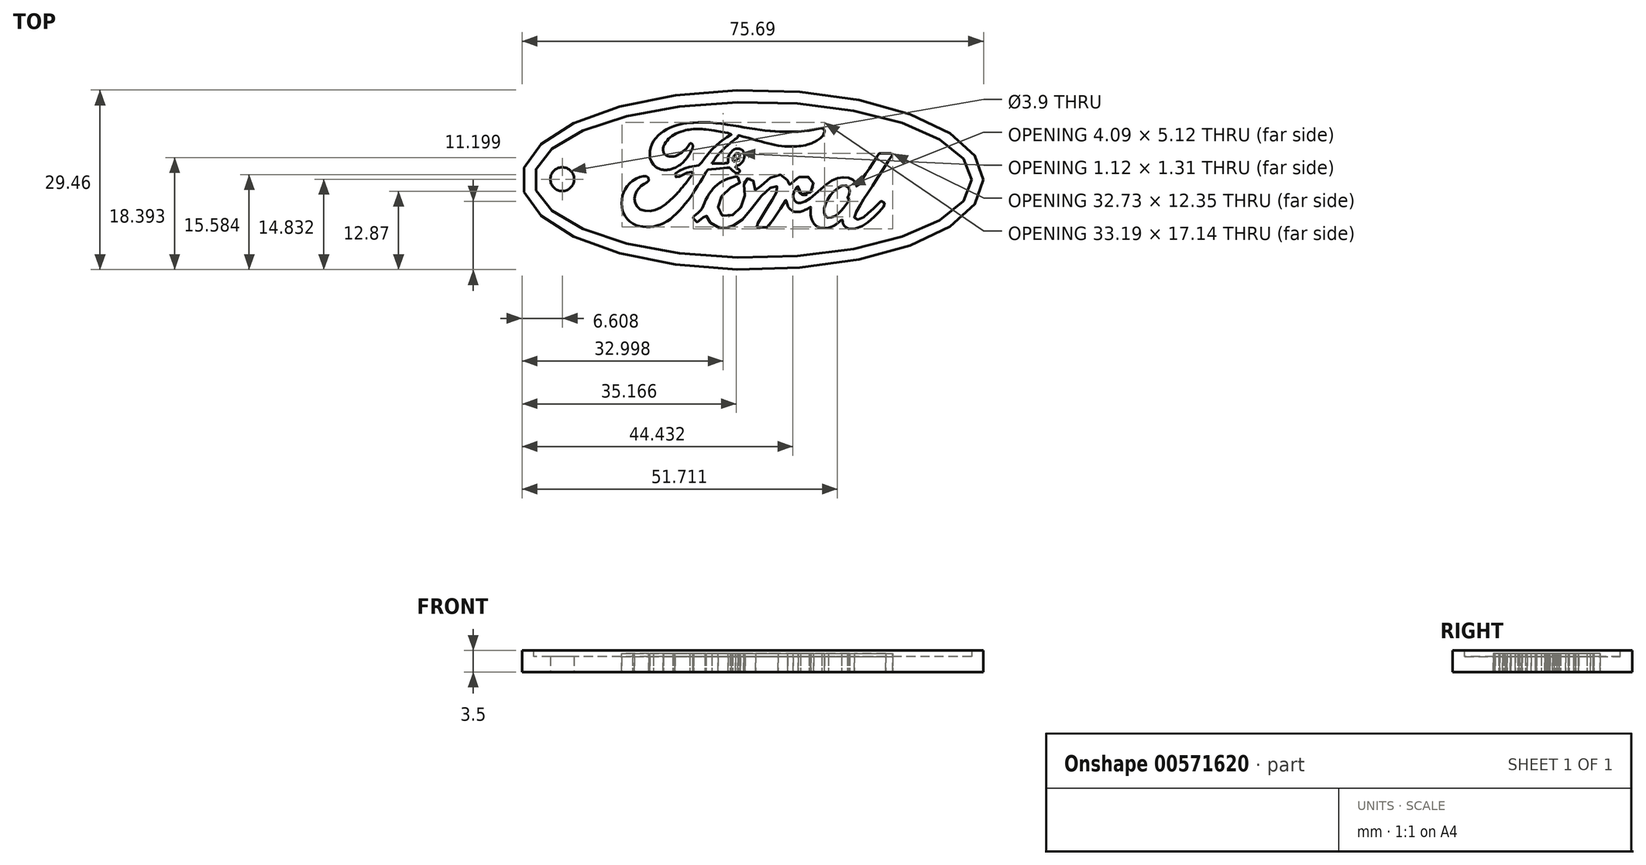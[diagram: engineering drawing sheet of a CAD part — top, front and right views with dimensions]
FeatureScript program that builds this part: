
annotation { "Feature Type Name" : "Feature", "Feature Type Description" : "" }
export const myFeature = defineFeature(function(context is Context, id is Id, definition is map)
    precondition{}
    {
        {
            var Q0;
            Q0=qCreatedBy(makeId("Top.planeOp"),FACE);
            var sketch = newSketch(context, id + "F0", { "sketchPlane" : qUnion([Q0])});
            skEllipse(sketch, "E0", {"center": v(49.35, 28.07) * mm, "majorRadius": 37.84 * mm, "minorRadius": 14.73 * mm, "majorAxis": v(1, 0)});
            skEllipse(sketch, "E1", {"center": v(49.35, 28.07) * mm, "majorRadius": 35.9 * mm, "minorRadius": 12.78 * mm, "majorAxis": v(1, 0)});
            skEllipse(sketch, "E2", {"center": v(49.35, 28.07) * mm, "majorRadius": 34.5 * mm, "minorRadius": 11.46 * mm, "majorAxis": v(1, 0)});
            skFitSpline(sketch, "E3", {"points": [v(39, 33.96) * mm, v(38.65, 33.42) * mm, v(37.9, 32.72) * mm, v(36.9, 32.06) * mm, v(36.02, 31.87) * mm, v(35.3, 32) * mm, v(34.74, 32.53) * mm, v(34.71, 33.54) * mm], "startDerivative": vector(-2.54, -4.41) * mm, "endDerivative": vector(0.86, 7.14) * mm});
            skFitSpline(sketch, "E4", {"points": [v(39, 33.96) * mm, v(39.05, 34.01) * mm, v(39.13, 34.04) * mm, v(39.22, 34.04) * mm, v(39.33, 34) * mm, v(39.41, 33.95) * mm, v(39.48, 33.85) * mm, v(39.52, 33.7) * mm, v(39.53, 33.58) * mm, v(39.51, 33.42) * mm, v(39.47, 33.25) * mm], "startDerivative": vector(0.5, 0.77) * mm, "endDerivative": vector(-0.4, -1.33) * mm});
            skFitSpline(sketch, "E5", {"points": [v(39.47, 33.25) * mm, v(39.38, 33.05) * mm, v(39.2, 32.68) * mm, v(39.06, 32.43) * mm, v(38.93, 32.22) * mm, v(38.79, 32) * mm, v(38.53, 31.64) * mm, v(38.31, 31.37) * mm, v(37.94, 30.96) * mm, v(37.5, 30.58) * mm, v(37.15, 30.34) * mm, v(36.73, 30.1) * mm, v(36.23, 29.9) * mm], "startDerivative": vector(-1.36, -2.97) * mm, "endDerivative": vector(-5.23, -2.02) * mm});
            skFitSpline(sketch, "E6", {"points": [v(36.23, 29.9) * mm, v(36.02, 29.83) * mm, v(35.62, 29.74) * mm, v(35.12, 29.7) * mm, v(34.65, 29.7) * mm, v(34.25, 29.8) * mm, v(33.78, 29.96) * mm, v(33.42, 30.23) * mm, v(33.06, 30.54) * mm], "startDerivative": vector(-2.14, -0.8) * mm, "endDerivative": vector(-2.8, 2.34) * mm});
            skFitSpline(sketch, "E7", {"points": [v(33.06, 30.54) * mm, v(32.87, 30.8) * mm, v(32.58, 31.42) * mm, v(32.5, 31.71) * mm, v(32.47, 32.08) * mm, v(32.47, 32.6) * mm, v(32.5, 32.94) * mm, v(32.6, 33.35) * mm, v(32.72, 33.73) * mm, v(32.9, 34.16) * mm, v(33.15, 34.52) * mm, v(33.4, 34.86) * mm, v(33.8, 35.29) * mm, v(34.05, 35.52) * mm, v(34.32, 35.72) * mm, v(34.58, 35.93) * mm, v(34.9, 36.13) * mm, v(35.32, 36.36) * mm, v(35.67, 36.53) * mm, v(36.14, 36.74) * mm, v(36.63, 36.92) * mm, v(37.04, 37.04) * mm, v(37.3, 37.12) * mm, v(37.67, 37.22) * mm, v(38.03, 37.28) * mm, v(38.4, 37.35) * mm, v(38.78, 37.38) * mm, v(39.14, 37.41) * mm, v(39.67, 37.44) * mm, v(40.22, 37.47) * mm, v(40.68, 37.48) * mm, v(41.09, 37.5) * mm, v(41.53, 37.5) * mm], "startDerivative": vector(-6.48, 7.74) * mm, "endDerivative": vector(14.01, -0.13) * mm});
            skFitSpline(sketch, "E8", {"points": [v(41.53, 37.5) * mm, v(41.84, 37.5) * mm, v(42.37, 37.45) * mm, v(42.84, 37.42) * mm, v(43.37, 37.36) * mm, v(43.76, 37.3) * mm, v(44.34, 37.25) * mm, v(44.92, 37.17) * mm, v(45.59, 37.07) * mm, v(46.15, 36.97) * mm, v(46.53, 36.9) * mm, v(47.04, 36.82) * mm, v(47.56, 36.73) * mm, v(47.96, 36.66) * mm, v(48.43, 36.59) * mm, v(48.95, 36.51) * mm, v(49.49, 36.44) * mm, v(49.85, 36.38) * mm, v(50.28, 36.3) * mm, v(50.76, 36.24) * mm, v(51.13, 36.2) * mm, v(51.49, 36.15) * mm, v(51.98, 36.1) * mm, v(52.43, 36.05) * mm, v(52.87, 36.01) * mm, v(53.18, 35.98) * mm, v(53.5, 35.97) * mm, v(53.87, 35.95) * mm, v(54.32, 35.94) * mm, v(54.77, 35.94) * mm, v(55.14, 35.94) * mm, v(55.42, 35.94) * mm, v(55.7, 35.94) * mm, v(56.13, 35.95) * mm, v(56.44, 35.96) * mm, v(56.66, 35.97) * mm, v(56.92, 35.99) * mm, v(57.53, 36.03) * mm, v(58.03, 36.08) * mm, v(58.43, 36.13) * mm, v(58.76, 36.18) * mm, v(59, 36.22) * mm, v(59.27, 36.27) * mm, v(59.5, 36.31) * mm, v(59.74, 36.36) * mm, v(59.93, 36.4) * mm, v(60.14, 36.44) * mm, v(60.65, 36.52) * mm], "startDerivative": vector(15.58, 0.37) * mm, "endDerivative": vector(12.01, -0.51) * mm});
            skFitSpline(sketch, "E9", {"points": [v(60.65, 36.52) * mm, v(60.76, 36.52) * mm, v(60.84, 36.49) * mm, v(60.9, 36.44) * mm, v(60.97, 36.39) * mm, v(61.04, 36.3) * mm, v(61.07, 36.22) * mm, v(61.1, 36.1) * mm, v(61.1, 35.95) * mm, v(61.1, 35.85) * mm, v(61.04, 35.67) * mm, v(60.95, 35.46) * mm, v(60.81, 35.27) * mm, v(60.72, 35.16) * mm, v(60.58, 35.02) * mm, v(60.42, 34.89) * mm, v(60.2, 34.72) * mm, v(60, 34.6) * mm, v(59.84, 34.5) * mm, v(59.69, 34.4) * mm, v(59.5, 34.3) * mm, v(59.31, 34.2) * mm, v(59.14, 34.13) * mm, v(58.92, 34.04) * mm, v(58.56, 33.9) * mm], "startDerivative": vector(3.4, 0.28) * mm, "endDerivative": vector(-3.98, -1.68) * mm});
            skFitSpline(sketch, "E10", {"points": [v(58.56, 33.9) * mm, v(58.35, 33.84) * mm, v(58.07, 33.77) * mm, v(57.54, 33.67) * mm, v(57.1, 33.62) * mm, v(56.58, 33.57) * mm, v(56.12, 33.53) * mm, v(55.07, 33.53) * mm, v(54.11, 33.6) * mm, v(53, 33.8) * mm, v(51.9, 34.04) * mm, v(50.74, 34.36) * mm, v(49.2, 34.77) * mm, v(47.16, 35.3) * mm, v(46.92, 35.34) * mm], "startDerivative": vector(-5.59, -1.45) * mm, "endDerivative": vector(-4.29, 0.33) * mm});
            skFitSpline(sketch, "E11", {"points": [v(46.92, 35.34) * mm, v(46.92, 35.08) * mm, v(46.85, 34.96) * mm, v(46.52, 34.77) * mm, v(46.23, 34.53) * mm, v(45.97, 34.34) * mm, v(45.45, 33.9) * mm, v(45.1, 33.6) * mm, v(44.65, 33.21) * mm, v(44.15, 32.71) * mm, v(43.8, 32.35) * mm, v(43.3, 31.72) * mm, v(43.04, 31.34) * mm, v(42.76, 30.9) * mm, v(42.66, 30.7) * mm], "startDerivative": vector(0.32, -5.23) * mm, "endDerivative": vector(-1.72, -3.44) * mm});
            skFitSpline(sketch, "E12", {"points": [v(42.66, 30.7) * mm, v(43.28, 30.77) * mm, v(44, 30.77) * mm, v(44.55, 30.77) * mm, v(44.83, 30.79) * mm, v(45.06, 30.8) * mm, v(45.27, 30.83) * mm, v(45.3, 30.84) * mm, v(45.31, 31.17) * mm, v(45.31, 31.57) * mm, v(45.48, 32.15) * mm, v(45.94, 32.73) * mm, v(46.55, 33.13) * mm, v(47.15, 33.17) * mm], "startDerivative": vector(6.55, 0.78) * mm, "endDerivative": vector(6.66, -0.32) * mm});
            skFitSpline(sketch, "E13", {"points": [v(47.15, 33.17) * mm, v(47.47, 33.05) * mm, v(47.86, 32.67) * mm, v(48.01, 32.21) * mm, v(47.98, 31.74) * mm, v(47.78, 31.2) * mm, v(47.44, 30.77) * mm, v(47.15, 30.55) * mm, v(46.8, 30.37) * mm, v(46.52, 30.25) * mm], "startDerivative": vector(3.19, -0.8) * mm, "endDerivative": vector(-2.79, -1.33) * mm});
            skFitSpline(sketch, "E14", {"points": [v(46.52, 30.25) * mm, v(46.52, 30.14) * mm, v(46.8, 29.93) * mm, v(47.03, 29.78) * mm, v(47.15, 29.66) * mm, v(47.25, 29.58) * mm, v(47.22, 29.38) * mm, v(47.03, 29.19) * mm, v(46.76, 29.15) * mm, v(46.42, 29.31) * mm, v(46.13, 29.53) * mm, v(45.86, 29.76) * mm, v(45.67, 29.95) * mm, v(45.61, 30.05) * mm], "startDerivative": vector(-0.59, -2.04) * mm, "endDerivative": vector(-0.87, 1.8) * mm});
            skFitSpline(sketch, "E15", {"points": [v(45.61, 30.05) * mm, v(45.41, 30.05) * mm, v(45.06, 30.05) * mm, v(44.63, 29.98) * mm, v(44.26, 29.95) * mm, v(43.7, 29.9) * mm, v(43.21, 29.83) * mm, v(42.53, 29.78) * mm, v(42.06, 29.71) * mm, v(41.92, 29.67) * mm, v(41.74, 29.37) * mm, v(41.5, 28.97) * mm, v(41.19, 28.44) * mm, v(40.99, 28.13) * mm, v(40.74, 27.74) * mm, v(40.33, 27.06) * mm, v(39.87, 26.39) * mm, v(39.59, 25.91) * mm, v(39.28, 25.45) * mm, v(38.97, 25.01) * mm, v(38.67, 24.62) * mm, v(38.17, 24.01) * mm, v(37.74, 23.49) * mm, v(37.39, 23.08) * mm, v(36.87, 22.57) * mm, v(36.46, 22.17) * mm, v(36.04, 21.81) * mm, v(35.72, 21.54) * mm, v(35.34, 21.28) * mm, v(34.65, 20.91) * mm], "startDerivative": vector(-8.68, -0.14) * mm, "endDerivative": vector(-17.37, -8.98) * mm});
            skFitSpline(sketch, "E16", {"points": [v(34.65, 20.91) * mm, v(34.31, 20.76) * mm, v(33.82, 20.6) * mm, v(33.29, 20.46) * mm, v(32.61, 20.35) * mm, v(32.01, 20.31) * mm, v(31.4, 20.36) * mm, v(30.81, 20.44) * mm, v(30.32, 20.59) * mm, v(29.86, 20.79) * mm, v(29.27, 21.19) * mm, v(28.86, 21.55) * mm, v(28.48, 22.05) * mm, v(28.24, 22.49) * mm, v(28.03, 22.96) * mm, v(27.93, 23.34) * mm, v(27.86, 23.94) * mm, v(27.88, 24.74) * mm, v(28, 25.46) * mm, v(28.16, 25.96) * mm, v(28.4, 26.45) * mm, v(28.73, 26.96) * mm, v(29.2, 27.48) * mm, v(29.63, 27.87) * mm], "startDerivative": vector(-9.1, -4.58) * mm, "endDerivative": vector(9.88, 8.35) * mm});
            skFitSpline(sketch, "E17", {"points": [v(29.63, 27.87) * mm, v(30.22, 28.25) * mm, v(30.65, 28.44) * mm, v(31.2, 28.62) * mm, v(31.5, 28.68) * mm, v(31.85, 28.65) * mm, v(32.09, 28.57) * mm, v(32.25, 28.4) * mm, v(32.3, 28.17) * mm, v(32.3, 27.92) * mm, v(32.09, 27.7) * mm, v(31.78, 27.55) * mm, v(31.48, 27.37) * mm, v(31.12, 27.1) * mm, v(30.89, 26.87) * mm, v(30.64, 26.62) * mm, v(30.36, 26.27) * mm, v(30.09, 25.66) * mm, v(29.98, 25.3) * mm, v(29.98, 24.6) * mm, v(30.19, 24.06) * mm, v(30.45, 23.61) * mm, v(31.01, 23.17) * mm, v(31.79, 22.96) * mm, v(32.77, 22.96) * mm, v(33.8, 23.3) * mm, v(34.9, 23.91) * mm, v(35.68, 24.6) * mm, v(36.4, 25.25) * mm], "startDerivative": vector(15.04, 10.13) * mm, "endDerivative": vector(14.75, 13.32) * mm});
            skFitSpline(sketch, "E18", {"points": [v(36.4, 25.25) * mm, v(36.83, 25.68) * mm, v(37.2, 26.09) * mm, v(37.5, 26.48) * mm, v(37.77, 26.8) * mm, v(38.08, 27.16) * mm, v(38.4, 27.56) * mm, v(38.78, 28.05) * mm, v(39.01, 28.4) * mm, v(39.32, 28.81) * mm, v(39.5, 29.07) * mm, v(39.65, 29.26) * mm], "startDerivative": vector(4.28, 4.12) * mm, "endDerivative": vector(2.4, 2.76) * mm});
            skFitSpline(sketch, "E19", {"points": [v(39.65, 29.26) * mm, v(39.65, 29.35) * mm, v(39.56, 29.35) * mm, v(39.4, 29.34) * mm, v(39.17, 29.33) * mm, v(38.87, 29.26) * mm, v(38.57, 29.2) * mm, v(38.22, 29.07) * mm, v(37.98, 28.96) * mm, v(37.7, 28.81) * mm, v(37.46, 28.67) * mm, v(37.28, 28.54) * mm, v(37.05, 28.46) * mm, v(36.82, 28.48) * mm, v(36.69, 28.61) * mm, v(36.6, 28.8) * mm, v(36.69, 29.1) * mm, v(36.97, 29.35) * mm, v(37.34, 29.57) * mm, v(37.77, 29.77) * mm, v(38.2, 29.93) * mm, v(38.63, 30.09) * mm, v(39.07, 30.18) * mm, v(39.44, 30.25) * mm, v(39.85, 30.34) * mm, v(40.18, 30.4) * mm, v(40.57, 30.46) * mm, v(40.66, 30.47) * mm, v(40.92, 30.83) * mm, v(41.12, 31.1) * mm, v(41.38, 31.46) * mm, v(41.67, 31.82) * mm, v(41.95, 32.21) * mm, v(42.26, 32.6) * mm, v(42.61, 32.99) * mm, v(43.3, 33.66) * mm, v(43.9, 34.2) * mm, v(44.41, 34.64) * mm, v(44.93, 34.98) * mm, v(45.37, 35.27) * mm, v(45.78, 35.46) * mm, v(45.9, 35.55) * mm, v(45.84, 35.65) * mm, v(45.18, 35.76) * mm, v(44.65, 35.84) * mm, v(44.06, 35.95) * mm, v(42.79, 36.2) * mm, v(41.68, 36.31) * mm], "startDerivative": vector(2.22, 10.5) * mm, "endDerivative": vector(-29.56, 1.9) * mm});
            skFitSpline(sketch, "E20", {"points": [v(41.68, 36.31) * mm, v(40.87, 36.38) * mm, v(39.87, 36.4) * mm, v(38.98, 36.31) * mm, v(38.32, 36.18) * mm, v(37.07, 35.8) * mm, v(35.98, 35.19) * mm, v(35.33, 34.53) * mm, v(34.83, 33.76) * mm, v(34.71, 33.54) * mm], "startDerivative": vector(-7.23, 0.72) * mm, "endDerivative": vector(-1.48, -3.14) * mm});
            skFitSpline(sketch, "E21", {"points": [v(39.58, 21.76) * mm, v(39.85, 21.35) * mm, v(40.1, 21.1) * mm, v(40.35, 21.17) * mm, v(41.05, 21.72) * mm, v(41.38, 22.07) * mm, v(41.6, 22.27) * mm, v(41.68, 22.29) * mm, v(41.78, 22.14) * mm, v(42.06, 21.5) * mm, v(42.41, 21.02) * mm, v(43.01, 20.54) * mm, v(43.93, 20.23) * mm, v(44.55, 20.13) * mm, v(45.25, 20.2) * mm, v(46.02, 20.48) * mm, v(46.84, 20.87) * mm, v(48.06, 22) * mm, v(49.68, 24.08) * mm, v(51.3, 25.98) * mm, v(52.28, 26.8) * mm, v(53, 27.09) * mm, v(53.33, 27) * mm, v(53.48, 26.72) * mm, v(53.36, 26.27) * mm, v(53.06, 25.69) * mm, v(52.67, 24.96) * mm, v(52.05, 23.98) * mm, v(51.51, 23.12) * mm, v(51, 22.26) * mm, v(50.6, 21.66) * mm, v(50.24, 21.06) * mm, v(49.86, 20.47) * mm, v(49.85, 20.36) * mm, v(49.95, 20.3) * mm, v(50.75, 20.28) * mm, v(51.9, 20.3) * mm, v(52.35, 20.91) * mm, v(53.5, 22.71) * mm, v(54.35, 24.02) * mm, v(54.82, 24.77) * mm, v(54.87, 24.75) * mm, v(54.93, 24.42) * mm, v(55.02, 24) * mm], "startDerivative": vector(13.97, -21.19) * mm, "endDerivative": vector(5.75, -22.39) * mm});
            skFitSpline(sketch, "E22", {"points": [v(55.02, 24) * mm, v(55.14, 23.67) * mm, v(55.4, 23.35) * mm, v(55.82, 23.01) * mm, v(56.38, 22.81) * mm, v(57.08, 22.84) * mm, v(57.76, 23.05) * mm, v(58.3, 23.29) * mm, v(58.74, 23.57) * mm], "startDerivative": vector(0.96, -3.28) * mm, "endDerivative": vector(3.43, 2.45) * mm});
            skFitSpline(sketch, "E23", {"points": [v(58.74, 23.57) * mm, v(58.87, 23.57) * mm, v(58.87, 23.34) * mm, v(58.82, 22.83) * mm, v(58.9, 21.92) * mm, v(59.14, 21.3) * mm, v(59.61, 20.66) * mm, v(60.2, 20.29) * mm, v(61.04, 20.13) * mm, v(61.76, 20.19) * mm, v(61.78, 20.2) * mm], "startDerivative": vector(3, 0.7) * mm, "endDerivative": vector(0.47, 0.4) * mm});
            skFitSpline(sketch, "E24", {"points": [v(61.78, 20.2) * mm, v(62.46, 20.44) * mm, v(63.28, 20.97) * mm, v(63.93, 21.5) * mm], "startDerivative": vector(2.18, 0.61) * mm, "endDerivative": vector(1.87, 1.59) * mm});
            skFitSpline(sketch, "E25", {"points": [v(63.93, 21.5) * mm, v(64.04, 21.5) * mm, v(64.1, 21.32) * mm, v(64.15, 20.93) * mm, v(64.4, 20.5) * mm, v(65.1, 20.04) * mm], "startDerivative": vector(1.12, 0.27) * mm, "endDerivative": vector(2.65, -1.42) * mm});
            skFitSpline(sketch, "E26", {"points": [v(65.1, 20.04) * mm, v(65.8, 20.04) * mm, v(66.75, 20.2) * mm, v(67.36, 20.5) * mm, v(68.1, 20.98) * mm, v(68.8, 21.6) * mm, v(69.65, 22.37) * mm, v(70.1, 22.87) * mm, v(70.7, 23.5) * mm, v(71.09, 24.02) * mm, v(71.13, 24.1) * mm, v(70.84, 24.34) * mm, v(70.56, 24.6) * mm, v(70.45, 24.6) * mm, v(70.25, 24.47) * mm, v(69.97, 24.18) * mm, v(69.48, 23.7) * mm, v(69.08, 23.28) * mm, v(68.65, 22.89) * mm, v(68.04, 22.39) * mm, v(67.54, 21.95) * mm, v(66.89, 21.62) * mm, v(66.47, 21.55) * mm, v(66.18, 21.65) * mm, v(66.01, 21.93) * mm, v(66.12, 22.44) * mm, v(66.55, 23.2) * mm, v(67.07, 24.04) * mm, v(67.47, 24.72) * mm, v(67.9, 25.4) * mm, v(68.49, 26.32) * mm, v(69.18, 27.37) * mm, v(70.08, 28.79) * mm, v(71.03, 30.26) * mm, v(71.8, 31.45) * mm, v(72.3, 32.24) * mm], "startDerivative": vector(23.12, -0.84) * mm, "endDerivative": vector(14.18, 22.97) * mm});
            skFitSpline(sketch, "E27", {"points": [v(39.58, 21.76) * mm, v(39.58, 21.9) * mm, v(39.75, 22.09) * mm, v(40.55, 22.8) * mm, v(41.2, 23.63) * mm, v(41.67, 24.8) * mm, v(42.53, 26.2) * mm, v(43.28, 27.06) * mm, v(44.25, 27.77) * mm, v(45.52, 28.32) * mm, v(46.45, 28.55) * mm, v(46.88, 28.55) * mm], "startDerivative": vector(-0.6, 3.95) * mm, "endDerivative": vector(6.23, -0.43) * mm});
            skFitSpline(sketch, "E28", {"points": [v(46.88, 28.55) * mm, v(47.08, 28.38) * mm, v(47.23, 28.03) * mm, v(47.33, 27.72) * mm, v(47.28, 27.61) * mm, v(46.88, 27.43) * mm, v(46.32, 27.2) * mm, v(45.66, 26.76) * mm, v(44.86, 26.14) * mm, v(44.23, 25.3) * mm, v(43.93, 24.68) * mm, v(43.73, 23.9) * mm, v(43.74, 23.04) * mm, v(43.95, 22.58) * mm, v(44.33, 22.2) * mm, v(45, 22.01) * mm, v(45.69, 22.12) * mm, v(46.36, 22.47) * mm, v(47.01, 23.09) * mm, v(47.4, 23.58) * mm, v(47.8, 24.44) * mm, v(48.02, 25.28) * mm, v(48.12, 26.07) * mm, v(48.06, 26.8) * mm, v(47.9, 27.56) * mm, v(47.89, 27.8) * mm, v(47.97, 27.98) * mm, v(48.38, 28.2) * mm, v(48.71, 28.39) * mm, v(48.95, 28.44) * mm, v(49.27, 28.26) * mm, v(49.47, 27.9) * mm, v(49.63, 27.44) * mm, v(49.76, 26.84) * mm, v(49.8, 26.32) * mm, v(49.88, 26.2) * mm, v(50.14, 26.46) * mm, v(50.65, 27) * mm, v(51.28, 27.65) * mm, v(52.01, 28.27) * mm, v(52.55, 28.55) * mm, v(53.27, 28.84) * mm, v(53.9, 28.9) * mm, v(54.5, 28.74) * mm, v(54.83, 28.44) * mm, v(55.02, 28) * mm, v(55.12, 27.56) * mm, v(55.12, 27.13) * mm, v(55.19, 27.07) * mm, v(55.57, 27.53) * mm, v(56.26, 28.16) * mm, v(57.05, 28.55) * mm, v(57.53, 28.68) * mm, v(58.1, 28.66) * mm, v(58.57, 28.5) * mm, v(58.93, 28.22) * mm, v(59.2, 27.85) * mm, v(59.3, 27.54) * mm, v(59.32, 27.08) * mm, v(59.17, 26.46) * mm, v(58.76, 25.94) * mm, v(58.23, 25.63) * mm, v(57.66, 25.6) * mm, v(57.16, 25.85) * mm, v(56.9, 26.2) * mm, v(56.83, 26.5) * mm, v(56.84, 26.86) * mm], "startDerivative": vector(20.96, -13.41) * mm, "endDerivative": vector(1.41, 30.16) * mm});
            skFitSpline(sketch, "E29", {"points": [v(56.84, 26.86) * mm, v(56.84, 26.94) * mm, v(56.77, 26.99) * mm, v(56.64, 26.9) * mm, v(56.44, 26.67) * mm, v(56.23, 26.32) * mm, v(56.13, 26.17) * mm, v(56.02, 25.67) * mm, v(56, 25.3) * mm, v(56.1, 24.87) * mm, v(56.4, 24.49) * mm, v(56.74, 24.3) * mm, v(57.22, 24.28) * mm], "startDerivative": vector(0.35, 2) * mm, "endDerivative": vector(4.77, 0.19) * mm});
            skFitSpline(sketch, "E30", {"points": [v(57.22, 24.28) * mm, v(57.8, 24.43) * mm, v(58.26, 24.7) * mm, v(59.1, 25.27) * mm, v(59.98, 26.06) * mm, v(61.09, 27) * mm, v(61.92, 27.66) * mm, v(62.83, 28.16) * mm, v(63.55, 28.41) * mm, v(64.31, 28.5) * mm, v(65.04, 28.42) * mm, v(65.55, 28.2) * mm, v(65.92, 27.94) * mm, v(66.26, 27.5) * mm, v(66.35, 27.23) * mm, v(66.4, 27.02) * mm, v(66.44, 26.94) * mm, v(66.59, 27.04) * mm, v(66.95, 27.6) * mm, v(67.53, 28.46) * mm, v(68.08, 29.3) * mm, v(68.66, 30.18) * mm, v(69.3, 31.15) * mm, v(69.9, 32.1) * mm, v(70.06, 32.34) * mm, v(70.11, 32.39) * mm, v(70.4, 32.38) * mm, v(70.7, 32.38) * mm, v(71.2, 32.38) * mm, v(71.61, 32.39) * mm, v(72.03, 32.38) * mm, v(72.23, 32.38) * mm, v(72.3, 32.33) * mm, v(72.3, 32.24) * mm], "startDerivative": vector(19.22, 3.8) * mm, "endDerivative": vector(-1.38, -8.02) * mm});
            skCircle(sketch, "E31", {"center": v(18.12, 28.17) * mm, "radius": 1.95 * mm});
            skFitSpline(sketch, "E32", {"points": [v(65.17, 24.9) * mm, v(64.96, 24.44) * mm, v(64.4, 23.68) * mm, v(63.87, 22.99) * mm, v(63.05, 22.26) * mm, v(62.35, 21.92) * mm, v(61.56, 21.89) * mm, v(61.14, 22.37) * mm, v(61.1, 23.4) * mm, v(61.6, 24.79) * mm, v(62.55, 26.04) * mm, v(63.74, 26.98) * mm, v(64.67, 27.08) * mm, v(65.2, 26.6) * mm, v(65.16, 25.7) * mm, v(64.9, 25.06) * mm, v(65.17, 24.9) * mm]});
            skFitSpline(sketch, "E33", {"points": [v(46.18, 31.08) * mm, v(46.41, 31.11) * mm, v(46.85, 31.44) * mm, v(47.23, 31.97) * mm, v(47.11, 32.37) * mm, v(46.75, 32.4) * mm, v(46.4, 32.14) * mm, v(46.14, 31.73) * mm, v(46.18, 31.08) * mm]});
            skSolve(sketch);
        }
        {
            var Q0;
            Q0=makeQuery(id+"F0.imprint","IMPRINT",FACE,{"disambiguationData":[TD([[makeQuery(id+"F0.imprint","IMPRINT",EDGE,{"derivedFrom":sQuery(id+"F0.wireOp",EDGE,"E2")}),1.0]])]});
            var Q1;
            Q1=makeQuery(id+"F0.imprint","IMPRINT",FACE,{"disambiguationData":[TD([[makeQuery(id+"F0.imprint","IMPRINT",EDGE,{"derivedFrom":sQuery(id+"F0.wireOp",EDGE,"E0")}),1.0]])]});
            var Q2;
            Q2=makeQuery(id+"F0.imprint","IMPRINT",FACE,{"disambiguationData":[TD([[makeQuery(id+"F0.imprint","IMPRINT",EDGE,{"derivedFrom":sQuery(id+"F0.wireOp",EDGE,"E1")}),1.0]])]});
            var Q3;
            Q3=makeQuery(id+"F0.imprint","IMPRINT",FACE,{"disambiguationData":[TD([[makeQuery(id+"F0.imprint","IMPRINT",EDGE,{"derivedFrom":sQuery(id+"F0.wireOp",EDGE,"E33")}),1.0]])]});
            var Q4;
            Q4=makeQuery(id+"F0.imprint","IMPRINT",FACE,{"disambiguationData":[TD([[makeQuery(id+"F0.imprint","IMPRINT",EDGE,{"derivedFrom":sQuery(id+"F0.wireOp",EDGE,"E32")}),-1.0]])]});
            extrude(context, id + "F1", {"entities" : qUnion([Q0, Q1, Q2, Q3, Q4]), "depth" : 2.5 * mm, "offsetDistance" : 25 * mm});
        }
        {
            var Q0;
            Q0=makeQuery(id+"F0.imprint","IMPRINT",FACE,{"disambiguationData":[TD([[makeQuery(id+"F0.imprint","IMPRINT",EDGE,{"derivedFrom":sQuery(id+"F0.wireOp",EDGE,"E3")}),1.0]])]});
            var Q1;
            Q1=makeQuery(id+"F0.imprint","IMPRINT",FACE,{"disambiguationData":[TD([[makeQuery(id+"F0.imprint","IMPRINT",EDGE,{"derivedFrom":sQuery(id+"F0.wireOp",EDGE,"E21")}),1.0]])]});
            extrude(context, id + "F2", {"entities" : qUnion([Q0, Q1]), "depth" : 3 * mm, "offsetDistance" : 25 * mm});
        }
        {
            var Q0;
            Q0=makeQuery(id+"F0.imprint","IMPRINT",FACE,{"disambiguationData":[TD([[makeQuery(id+"F0.imprint","IMPRINT",EDGE,{"derivedFrom":sQuery(id+"F0.wireOp",EDGE,"E31")}),1.0]])]});
            extrude(context, id + "F3", {"entities" : qUnion([Q0]), "operationType" : NewBodyOperationType.REMOVE, "depth" : 3 * mm, "offsetDistance" : 25 * mm});
        }
        {
            var Q0;
            Q0=makeQuery(id+"F0.imprint","IMPRINT",FACE,{"disambiguationData":[TD([[makeQuery(id+"F0.imprint","IMPRINT",EDGE,{"derivedFrom":sQuery(id+"F0.wireOp",EDGE,"E0")}),1.0]])]});
            extrude(context, id + "F4", {"entities" : qUnion([Q0]), "operationType" : NewBodyOperationType.ADD, "depth" : 3.5 * mm, "offsetDistance" : 25 * mm});
        }
    });
